# Revit family: Скамейка кованая «Вена»
name_source: partatom
category: Мебель
revit_build: Autodesk Revit 2017 (Build: 20160225_1515(x64)
units: mm (PartAtom-declared; Revit-internal decimal feet)

## family parameters
Всегда вертикально = Да
Заголовок OmniClass = General Furniture and Specialties
На основе рабочей плоскости = Нет
Номер OmniClass = 23.40.20.00
Общий = Нет
При загрузке вырезать с полостями = Нет
Точка расчета площади = Нет

## types (7) — shared parameters
ADSK_Код изделия = 8313
ADSK_Материал доски = <По категории>
ADSK_Материал опоры = <По категории>
ADSK_Материал фурнитуры = <По категории>
ADSK_Размер_Высота = 820 мм
ADSK_Размер_Высота сидения = 460 мм
ADSK_Размер_Высота спинки = 390 мм
ADSK_Размер_Ширина = 630 мм
ADSK_Размер_Ширина сидения = 390 мм
URL = https://hobbyka.ru
Изготовитель = ООО "Хоббика"

## per-type parameters (varying)
| type | ADSK_Размер_Длина | С_Количество_опор_Видимость | Стоимость |
| Скамейка кованая «Вена» 1.2м | 1200 мм | Нет | 6510 $ |
| Скамейка кованая «Вена» 1,5м | 1500 мм | Нет | 7508 $ |
| Скамейка кованая «Вена» 1,8м | 1800 мм | Нет | 8610 $ |
| Скамейка кованая «Вена» 2,0м (2 опоры) | 2000 мм | Нет | 9135 $ |
| Скамейка кованая «Вена» 2,0м | 2000 мм | Да | 12075 $ |
| Скамейка кованая «Вена» 3,0м | 3000 мм | Да | 13075 $ |
| Скамейка кованая «Вена» Кресло | 600 мм | Нет | 6143 $ |

note: column(s) folded — value = type name in every type: ADSK_Наименование
